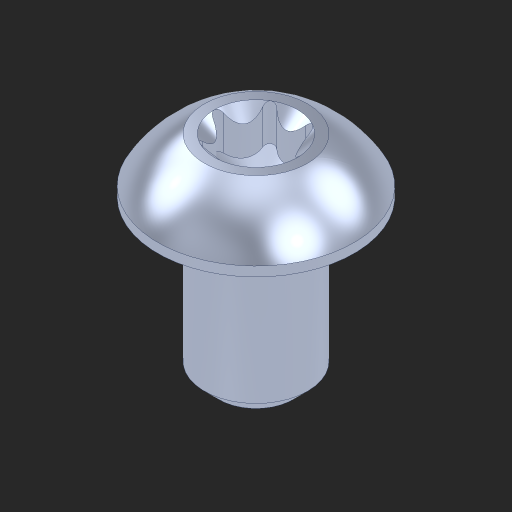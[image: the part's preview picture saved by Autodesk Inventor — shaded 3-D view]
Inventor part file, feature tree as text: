
AUTODESK INVENTOR PART (.ipt)
format: ipt  version: 2023 (Build 270158000, 158)  size: 342,528 bytes
history: native  units: in
note: dims shown in document units (in); Inventor stores cm internally (conversion verified against a paired STEP export)
features: other x58, sketch x5, extrude x1, thread x1, projected_geometry x1
ambient origin geometry x8: Origin, YZ Plane, XZ Plane, XY Plane, X Axis, Y Axis, Z Axis, Center Point
bodies: Solid1 (feature_tree), Body (feature_tree)
feature tree (66):
  other  "Table"
  other  "SScrew Star Smooth .250"
  other  "SScrew Star Smooth .290"
  other  "SScrew Star Smooth .375"
  other  "SScrew Star Smooth .500"
  other  "SScrew Star Smooth .625"
  other  "SScrew Star Smooth .750"
  other  "SScrew Star Smooth .875"
  other  "SScrew Star Smooth 1.000"
  other  "SScrew Star Smooth 1.250"
  other  "SScrew Star Smooth 1.500"
  other  "SScrew Star Smooth 1.750"
  other  "SScrew Star Smooth 2.000"
  other  "SScrew Star Smooth 2.250"
  other  "SScrew Star Smooth 2.500"
  other  "SScrew Star Threaded .250"
  other  "SScrew Star Threaded .290"
  other  "SScrew Star Threaded .375"
  other  "SScrew Star Threaded .500"
  other  "SScrew Star Threaded .625"
  other  "SScrew Star Threaded .750"
  other  "SScrew Star Threaded .875"
  other  "SScrew Star Threaded 1.000"
  other  "SScrew Star Threaded 1.250"
  other  "SScrew Star Threaded 1.500"
  other  "SScrew Star Threaded 1.750"
  other  "SScrew Star Threaded 2.000"
  other  "SScrew Star Threaded 2.250"
  other  "SScrew Star Threaded 2.500"
  other  "SScrew Star Smooth .290 - Color"
  other  "SScrew Star Smooth .375 - Color"
  other  "SScrew Star Smooth .500 - Color"
  other  "SScrew Star Smooth .625 - Color"
  other  "SScrew Star Smooth .750 - Color"
  other  "SScrew Star Smooth .875 - Color"
  other  "SScrew Star Smooth 1.000 - Color"
  other  "SScrew Star Smooth 1.250 - Color"
  other  "SScrew Star Smooth 1.500 - Color"
  other  "SScrew Star Smooth 1.750 - Color"
  other  "SScrew Star Smooth 2.000 - Color"
  other  "SScrew Star Smooth 2.250 - Color"
  other  "SScrew Star Smooth 2.500 - Color"
  other  "SScrew Star Threaded .290 - Color"
  other  "SScrew Star Threaded .375 - Color"
  other  "SScrew Star Threaded .500 - Color"
  other  "SScrew Star Threaded .625 - Color"
  other  "SScrew Star Threaded .750 - Color"
  other  "SScrew Star Threaded .875 - Color"
  other  "SScrew Star Threaded 1.000 - Color"
  other  "SScrew Star Threaded 1.250 - Color"
  other  "SScrew Star Threaded 1.500 - Color"
  other  "SScrew Star Threaded 1.750 - Color"
  other  "SScrew Star Threaded 2.000 - Color"
  other  "SScrew Star Threaded 2.250 - Color"
  other  "SScrew Star Threaded 2.500 - Color"
  other  "Head"
  extrude  "Hex"  Depth=0.164in
  other  "Head Chamfer"
  thread  "Thread"  [1 undecoded]
  other  "Tapered End"
  sketch  "Sketch1"  dims[d1=0.0in d4=0.164in d5=0.156in]
  sketch  "Sketch2"  dims[d6=0.015in]
  sketch  "Sketch4"  dims[d13=0.004in]
  sketch  "Sketch5"  dims[d14=0.082in]
  sketch  "Sketch6"  dims[d15=0.087in d16=0.0in d17=0.066in d20=90.0deg d22=0.07in d23=0.0in d29=0.066in d30=90.0deg d31=30.0deg d32=60.0deg d37=0.031in d38=0.275in d39=11.811in d40=0.0in d41=90.0deg d42=90.0deg d43=0.0in d44=0.0in d46=0.0312in d49=0.0585in d50=135.0deg d53=90.0deg d54=0.0027in d55=0.0205in d56=0.0039in d57=0.1378in d58=0.115in d59=0.163in d60=1.1811in d62=120.0deg]
  projected_geometry  "Projected Loop1"
note: 1 required parameter value undecoded (feature->parameter linkage not recoverable at this tier; creation-order binding heuristic only, values carry confidence <= 0.55)
